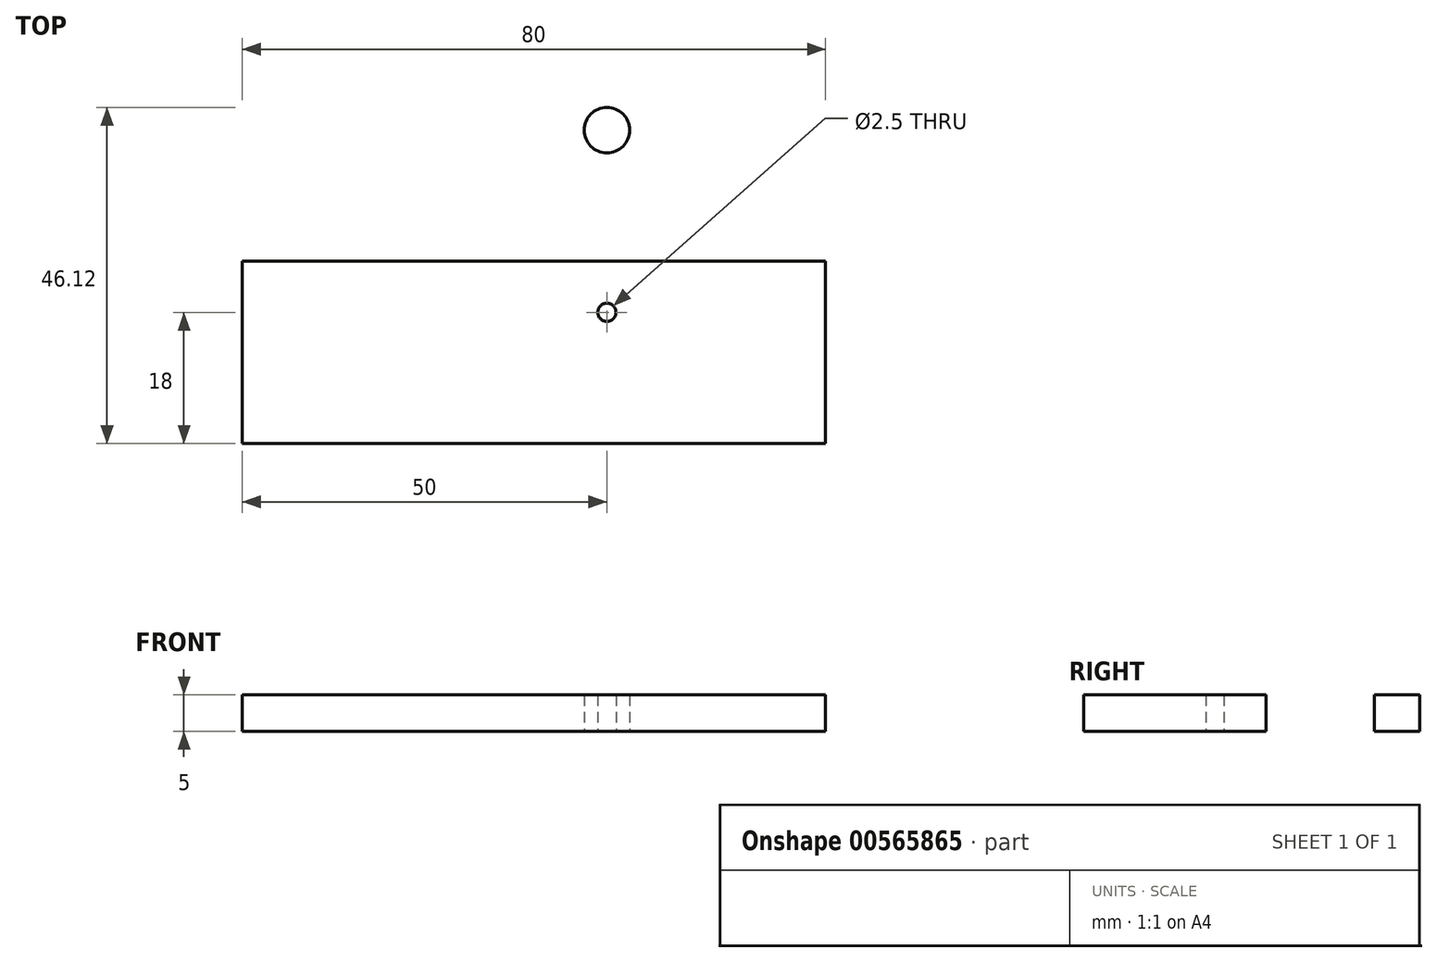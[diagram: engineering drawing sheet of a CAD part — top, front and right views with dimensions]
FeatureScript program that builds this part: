
annotation { "Feature Type Name" : "Feature", "Feature Type Description" : "" }
export const myFeature = defineFeature(function(context is Context, id is Id, definition is map)
    precondition{}
    {
        {
            var Q0;
            Q0=qCreatedBy(makeId("Top.planeOp"),FACE);
            var sketch = newSketch(context, id + "F0", { "sketchPlane" : qUnion([Q0])});
            skLineSegment(sketch, "E0.bottom", {"start": v(-40, 12.5) * mm, "end": v(40, 12.5) * mm});
            skLineSegment(sketch, "E0.top", {"start": v(-40, -12.5) * mm, "end": v(40, -12.5) * mm});
            skLineSegment(sketch, "E0.left", {"start": v(-40, 12.5) * mm, "end": v(-40, -12.5) * mm});
            skLineSegment(sketch, "E0.right", {"start": v(40, 12.5) * mm, "end": v(40, -12.5) * mm});
            skPoint(sketch, "E0.middle", {"position": v(0, 0) * mm});
            skLineSegment(sketch, "E1.bottom", {"start": v(-40, 12.5) * mm, "end": v(15, 12.5) * mm});
            skLineSegment(sketch, "E1.top", {"start": v(-40, 47.5) * mm, "end": v(15, 47.5) * mm});
            skLineSegment(sketch, "E1.left", {"start": v(-40, 12.5) * mm, "end": v(-40, 47.5) * mm});
            skLineSegment(sketch, "E1.right", {"start": v(15, 12.5) * mm, "end": v(15, 47.5) * mm});
            skCircle(sketch, "E2", {"center": v(10, 30.5) * mm, "radius": 3.12 * mm});
            skCircle(sketch, "E3", {"center": v(10, 5.5) * mm, "radius": 3.61 * mm});
            skSolve(sketch);
        }
        {
            var Q0;
            Q0=makeQuery(id+"F0.imprint","IMPRINT",FACE,{"disambiguationData":[TD([[makeQuery(id+"F0.imprint","IMPRINT",EDGE,{"derivedFrom":sQuery(id+"F0.wireOp",EDGE,"E0.bottom")}),-1.0]])]});
            var Q1;
            Q1=makeQuery(id+"F0.imprint","IMPRINT",FACE,{"disambiguationData":[TD([[makeQuery(id+"F0.imprint","IMPRINT",EDGE,{"derivedFrom":sQuery(id+"F0.wireOp",EDGE,"E1.bottom")}),1.0]])]});
            var Q2;
            Q2=makeQuery(id+"F0.imprint","IMPRINT",FACE,{"disambiguationData":[TD([[makeQuery(id+"F0.imprint","IMPRINT",EDGE,{"derivedFrom":sQuery(id+"F0.wireOp",EDGE,"E2")}),1.0]])]});
            var Q3;
            Q3=makeQuery(id+"F0.imprint","IMPRINT",FACE,{"disambiguationData":[TD([[makeQuery(id+"F0.imprint","IMPRINT",EDGE,{"derivedFrom":sQuery(id+"F0.wireOp",EDGE,"E3")}),1.0]])]});
            extrude(context, id + "F1", {"entities" : qUnion([Q0, Q1, Q2, Q3]), "depth" : 5 * mm, "offsetDistance" : 25 * mm});
        }
        {
            var Q0;
            Q0=sQuery(id+"F0.wireOp",VERTEX,"E2.center");
            var Q1;
            Q1=sQuery(id+"F0.wireOp",VERTEX,"E3.center");
            var Q2;
            Q2=makeQuery(id+"F1.opExtrude","SWEPT_BODY",BODY,{"disambiguationData":[OSD([sQuery(id+"F0.wireOp",EDGE,"E0.bottom"),sQuery(id+"F0.wireOp",EDGE,"E0.top"),sQuery(id+"F0.wireOp",EDGE,"E0.left"),sQuery(id+"F0.wireOp",EDGE,"E0.right"),sQuery(id+"F0.wireOp",EDGE,"E1.top"),sQuery(id+"F0.wireOp",EDGE,"E1.left"),sQuery(id+"F0.wireOp",EDGE,"E1.right")])]});
            hole(context, id + "F2", {"style" : HoleStyle.SIMPLE, "endStyle" : HoleEndStyle.THROUGH, "oppositeDirection" : true, "standardTappedOrClearance" : lookupTablePath({ "standard" : "ISO", "engagement" : "75%", "pitch" : "0.5 mm", "size" : "M3", "type" : "Tapped" }), "standardBlindInLast" : lookupTablePath({ "standard" : "ISO", "engagement" : "75%", "pitch" : "0.5 mm", "size" : "M3", "type" : "Tapped" }), "holeDiameter" : 2.5 * mm, "showTappedDepth" : true, "isTappedThrough" : true, "tappedDepth" : 2.5 * mm, "tapClearance" : 3, "locations" : qUnion([Q0, Q1]), "scope" : qUnion([Q2]), "majorDiameter" : 3 * mm});
        }
    });
